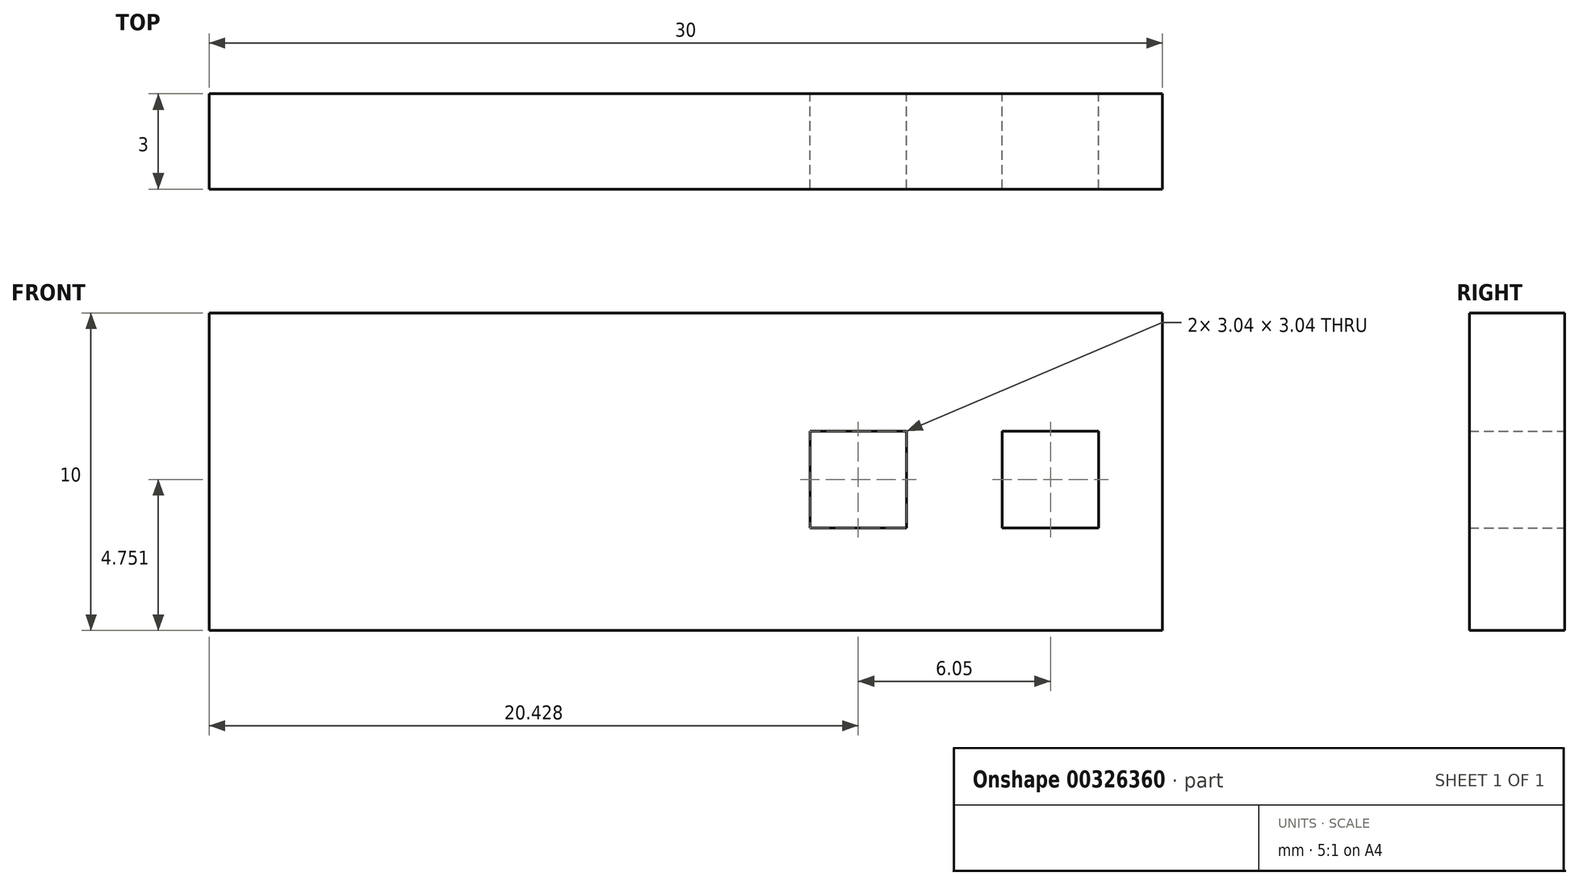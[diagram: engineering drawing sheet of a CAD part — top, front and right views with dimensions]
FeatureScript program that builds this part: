
annotation { "Feature Type Name" : "Feature", "Feature Type Description" : "" }
export const myFeature = defineFeature(function(context is Context, id is Id, definition is map)
    precondition{}
    {
        {
            var Q0;
            Q0=qCreatedBy(makeId("Front.planeOp"),FACE);
            var sketch = newSketch(context, id + "F0", { "sketchPlane" : qUnion([Q0])});
            skLineSegment(sketch, "E0.bottom", {"start": v(-9.73, 0) * mm, "end": v(20.27, 0) * mm});
            skLineSegment(sketch, "E0.top", {"start": v(-9.73, 10) * mm, "end": v(20.27, 10) * mm});
            skLineSegment(sketch, "E0.left", {"start": v(-9.73, 0) * mm, "end": v(-9.73, 10) * mm});
            skLineSegment(sketch, "E0.right", {"start": v(20.27, 0) * mm, "end": v(20.27, 10) * mm});
            skLineSegment(sketch, "E1.bottom", {"start": v(12.22, 6.27) * mm, "end": v(9.18, 6.27) * mm});
            skLineSegment(sketch, "E1.top", {"start": v(12.22, 3.23) * mm, "end": v(9.18, 3.23) * mm});
            skLineSegment(sketch, "E1.left", {"start": v(12.22, 6.27) * mm, "end": v(12.22, 3.23) * mm});
            skLineSegment(sketch, "E1.right", {"start": v(9.18, 6.27) * mm, "end": v(9.18, 3.23) * mm});
            skLineSegment(sketch, "E2.bottom", {"start": v(15.23, 6.27) * mm, "end": v(18.27, 6.27) * mm});
            skLineSegment(sketch, "E2.top", {"start": v(15.23, 3.23) * mm, "end": v(18.27, 3.23) * mm});
            skLineSegment(sketch, "E2.left", {"start": v(15.23, 6.27) * mm, "end": v(15.23, 3.23) * mm});
            skLineSegment(sketch, "E2.right", {"start": v(18.27, 6.27) * mm, "end": v(18.27, 3.23) * mm});
            skSolve(sketch);
        }
        {
            var Q0;
            Q0=makeQuery(id+"F0.imprint","IMPRINT",FACE,{"disambiguationData":[TD([[makeQuery(id+"F0.imprint","IMPRINT",EDGE,{"derivedFrom":sQuery(id+"F0.wireOp",EDGE,"E0.bottom")}),1.0]])]});
            extrude(context, id + "F1", {"entities" : qUnion([Q0]), "depth" : 3 * mm});
        }
    });
